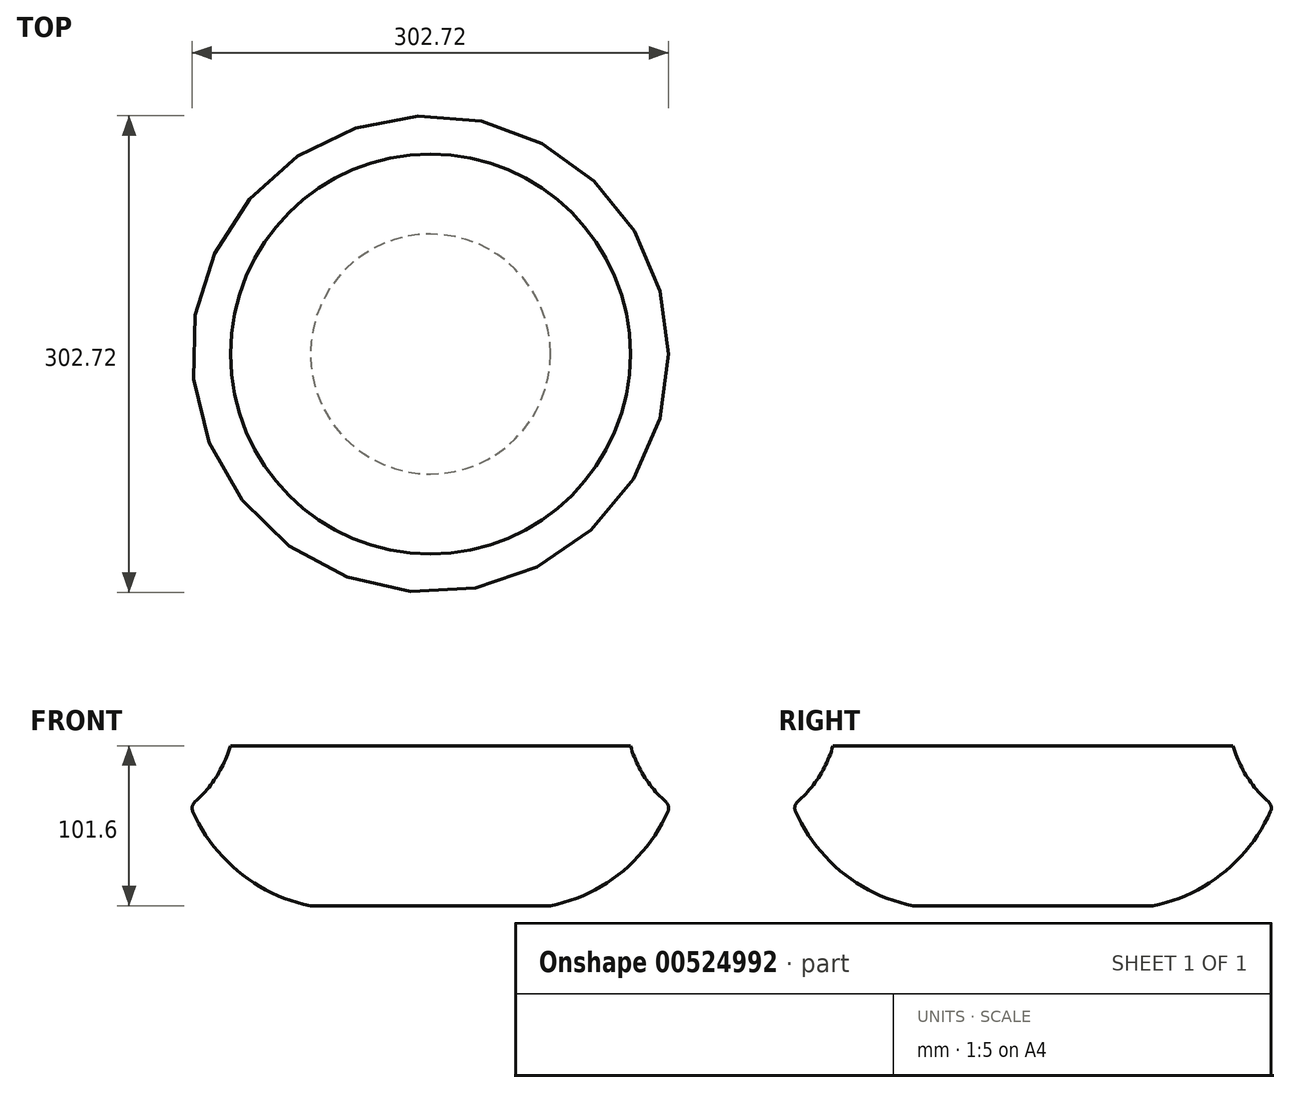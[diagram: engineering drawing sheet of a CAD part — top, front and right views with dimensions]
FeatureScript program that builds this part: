
annotation { "Feature Type Name" : "Feature", "Feature Type Description" : "" }
export const myFeature = defineFeature(function(context is Context, id is Id, definition is map)
    precondition{}
    {
        {
            var Q0;
            Q0=qCreatedBy(makeId("Front.planeOp"),FACE);
            var sketch = newSketch(context, id + "F0", { "sketchPlane" : qUnion([Q0])});
            skLineSegment(sketch, "E0", {"start": v(0, 0) * mm, "end": v(0, 101.6) * mm, "construction": true});
            skLineSegment(sketch, "E1", {"start": v(0, 0) * mm, "end": v(-152.4, 0) * mm, "construction": true});
            skLineSegment(sketch, "E2", {"start": v(0, 101.6) * mm, "end": v(-76.2, 101.6) * mm, "construction": true});
            skLineSegment(sketch, "E3", {"start": v(-152.4, 0) * mm, "end": v(-152.4, 63.5) * mm, "construction": true});
            skLineSegment(sketch, "E4", {"start": v(0, 0) * mm, "end": v(-76.2, 0) * mm});
            skArc(sketch, "E5", {"start": v(-152.4, 63.5) * mm, "mid": v(-122.33, 22.11) * mm, "end": v(-76.2, 0) * mm});
            skLineSegment(sketch, "E6", {"start": v(0, 101.6) * mm, "end": v(-127, 101.6) * mm});
            skArc(sketch, "E7", {"start": v(-152.4, 63.5) * mm, "mid": v(-136.82, 80.63) * mm, "end": v(-127, 101.6) * mm});
            skLineSegment(sketch, "E8", {"start": v(0, 0) * mm, "end": v(0, 101.6) * mm});
            skSolve(sketch);
        }
        {
            var Q0;
            Q0=makeQuery(id+"F0.imprint","IMPRINT",FACE,{"disambiguationData":[TD([[makeQuery(id+"F0.imprint","IMPRINT",EDGE,{"derivedFrom":sQuery(id+"F0.wireOp",EDGE,"E4")}),-1.0]])]});
            var Q1;
            Q1=sQuery(id+"F0.wireOp",EDGE,"E8");
            revolve(context, id + "F1", {"entities" : qUnion([Q0]), "axis" : qUnion([Q1]), "revolveType" : RevolveType.FULL});
        }
        {
            var Q0;
            Q0=makeQuery(id+"F1.opRevolve","SWEPT_EDGE",EDGE,{"disambiguationData":[OSD([sQuery(id+"F0.wireOp",EDGE,"E5"),sQuery(id+"F0.wireOp",EDGE,"E7")])]});
            fillet(context, id + "F2", {"entities" : qUnion([Q0]), "radius" : 5.08 * mm, "tangentPropagation" : true, "allowEdgeOverflow" : false});
        }
    });
